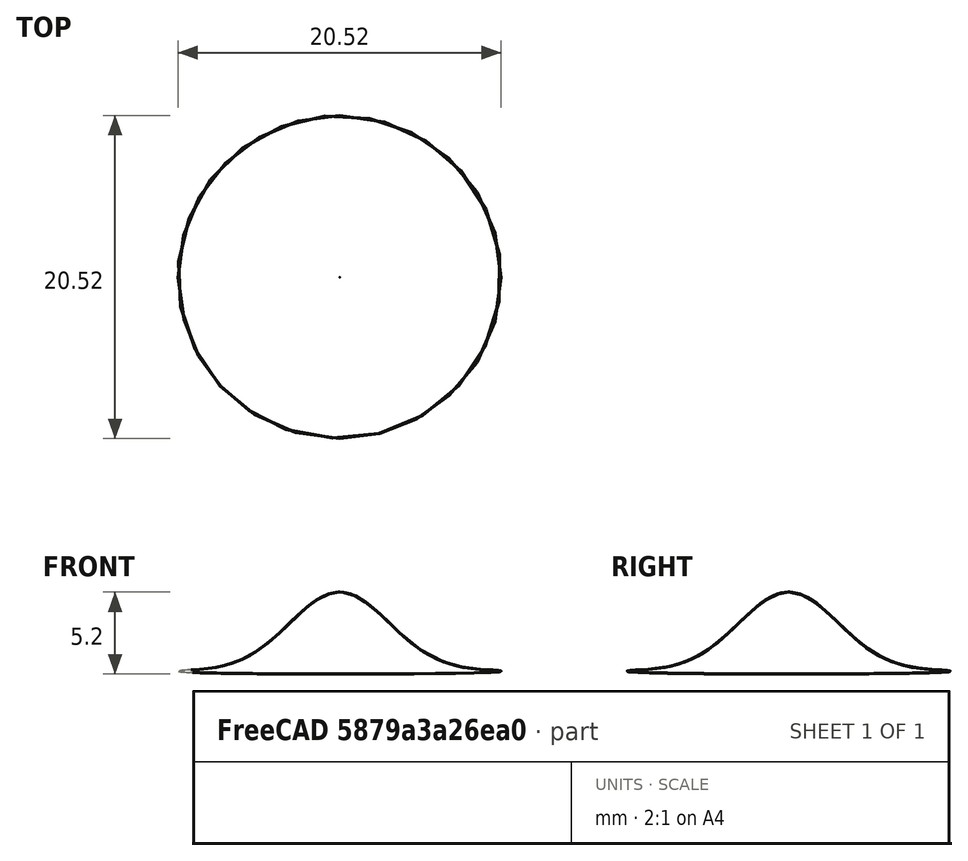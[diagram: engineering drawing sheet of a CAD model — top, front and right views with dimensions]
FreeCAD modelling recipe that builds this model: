
FCSTD DOCUMENT  (FreeCAD 1.0RUnknown)
Label: parametric-curves-gaussian
License: All rights reserved
LicenseURL: https://en.wikipedia.org/wiki/All_rights_reserved
objects: Part::FeaturePython×1, PartDesign::SubShapeBinder×1, PartDesign::Revolution×1, Sketcher::SketchObject×1, PartDesign::Body×1
note: 8 computed .brp shape members not serialized (recipe doc carries the construction recipe); baked Part::Feature solids carry a one-line shape summary decoded from their .brp

FEATURE [Part::FeaturePython] ParametricCurve  # WARN: FeaturePython — macro-defined, semantics opaque (R4)
  AttacherType = Attacher::AttachEngine3D
  Closed = true
  Continuity = C2
  EditFormulas = false
  F_X = 0.001
  F_Y = 0
  F_Z = 0
  F_a = 0
  F_b = 0
  F_c = 0
  F_d = [0,0]
  FormulaName = formula1
  Formulas = 9
  Interval = 0.1
  MakeFace = false
  PlusOneIteration = true
  Points = (190) [(0.001,-9.42478,0.0589018),(0.001,-9.32478,0.0646908),(0.001,-9.22478,0.0709778),(0.001,-9.12478,0.0777979),(0.001,-9.02478,0.0851881),+185 more]
  ShapeType = 0
  Sorted = false
  UpdateSpreadsheet = false
  UseSpreadsheet = false
  Version = 2025.05.08
  X = 0.001
  Y = t
  Z = 5 * exp(-0.05*t*t )
  t_max = 9.42478
  t_min = -9.42478
FEATURE [PartDesign::SubShapeBinder] Binder
  BindCopyOnChange = 0
  BindMode = 0
  ClaimChildren = false
  Context = -> Body [Binder.]
  Fuse = false
  MakeFace = true
  OffsetFill = false
  OffsetIntersection = false
  OffsetJoinType = 0
  OffsetOpenResult = false
  PartialLoad = false
  Refine = true
  Relative = true
  Support = -> [ParametricCurve]
  _Version = 2
FEATURE [PartDesign::Revolution] Revolution
  Angle = 360
  Angle2 = 60
  Axis = (1e-16,1e-16,1)
  Base = (0,0,0)
  Profile = -> Binder
  ReferenceAxis = -> Z_Axis
  Refine = true
  Reversed = true
  Suppressed = false
  Type = 0
FEATURE [Sketcher::SketchObject] Sketch
  ArcFitTolerance = 1e-06
  AttachmentSupport = -> [YZ_Plane]
  ExternalGeometry = -> [Binder]
  FullyConstrained = false
  MakeInternals = false
  MapMode = 5
  Placement = pos=(0,0,0) rot=(0.57735,0.57735,0.57735;2.0944rad)
  sketch-geometry (4):
    g0: LineSegment StartX=-10.2579 StartY=-0.0244087 StartZ=0 EndX=-10.2579 EndY=-13.607 EndZ=0
    g1: LineSegment StartX=-10.2579 StartY=-13.607 StartZ=0 EndX=10.2429 EndY=-13.607 EndZ=0
    g2: LineSegment StartX=10.2429 StartY=-13.607 StartZ=0 EndX=10.2429 EndY=-0.0244087 EndZ=0
    g3: LineSegment StartX=10.2429 StartY=-0.0244087 StartZ=0 EndX=-10.2579 EndY=-0.0244087 EndZ=0
  constraints (10):
    c: PointOnObject(g0,g-3)
    c: Vertical(g0)
    c: Coincident(g0,g1)
    c: Horizontal(g1)
    c: Coincident(g1,g2)
    c: PointOnObject(g2,g-3)
    c: Coincident(g2,g3)
    c: Coincident(g3,g0)
    c: Horizontal(g3)
    c: Vertical(g2)
FEATURE [PartDesign::Body] Body
  AllowCompound = false
  Group = -> [Binder,Revolution,Sketch]
  Origin = -> Origin
  Tip = -> Revolution
